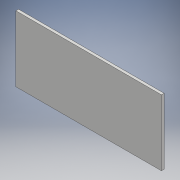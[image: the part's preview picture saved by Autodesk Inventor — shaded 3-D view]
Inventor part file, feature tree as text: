
AUTODESK INVENTOR PART (.ipt)
format: ipt  version: 2018 (Build 220112000, 112)  size: 87,040 bytes
history: native  units: mm
features: other x1, extrude x1, sketch x1
ambient origin geometry x8: Origin, YZ Plane, XZ Plane, XY Plane, X Axis, Y Axis, Z Axis, Center Point
bodies: Body1 (feature_tree)
feature tree (3):
  other  "ソリッド1"
  extrude  "押し出し1"  Depth=219.0mm
  sketch  "スケッチ1"
